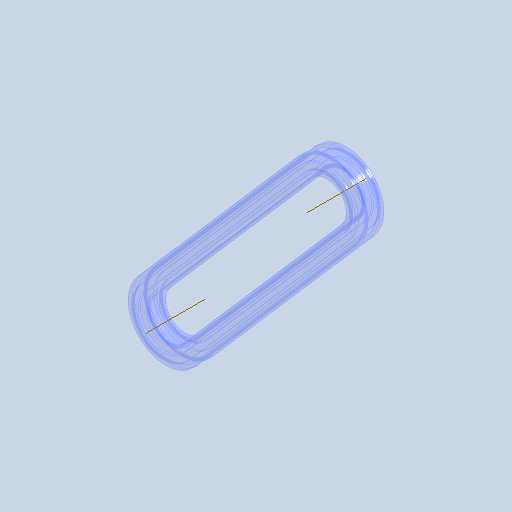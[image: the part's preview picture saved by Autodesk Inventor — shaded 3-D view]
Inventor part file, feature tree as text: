
AUTODESK INVENTOR PART (.ipt)
format: ipt  version: 2022.1 (Build 261234000, 234)  size: 176,640 bytes
history: native  units: mm
features: other x4, plane x2, sweep x1, pattern_linear x1, sketch x1
ambient origin geometry x8: Origin, YZ Plane, XZ Plane, XY Plane, X Axis, Y Axis, Z Axis, Center Point
bodies: Solid1 (feature_tree)
feature tree (9):
  other  "Eje de trabajo1"
  other  "Eje de trabajo2"
  plane  "Plano de trabajo2"
  plane  "Plano de trabajo3"
  other  "Trayectoria"
  other  "Plano de sección"
  sweep  "Sólido"
  pattern_linear  "Strand Pattern"  Spacing1=5.08mm  [1 undecoded]
  sketch  "Boceto de sección"  dims[d2=0.0mm d4=0.0mm d21=5.08mm d22=10.16mm d23=9.65mm d24=3.0mm d28=10.0mm d30=16.59mm d31=14.73mm d32=19.6mm d33=0.0mm d34=0.0mm d35=0.0mm d36=0.0mm d37=0.0mm]
note: 1 required parameter value undecoded (feature->parameter linkage not recoverable at this tier; creation-order binding heuristic only, values carry confidence <= 0.55)
